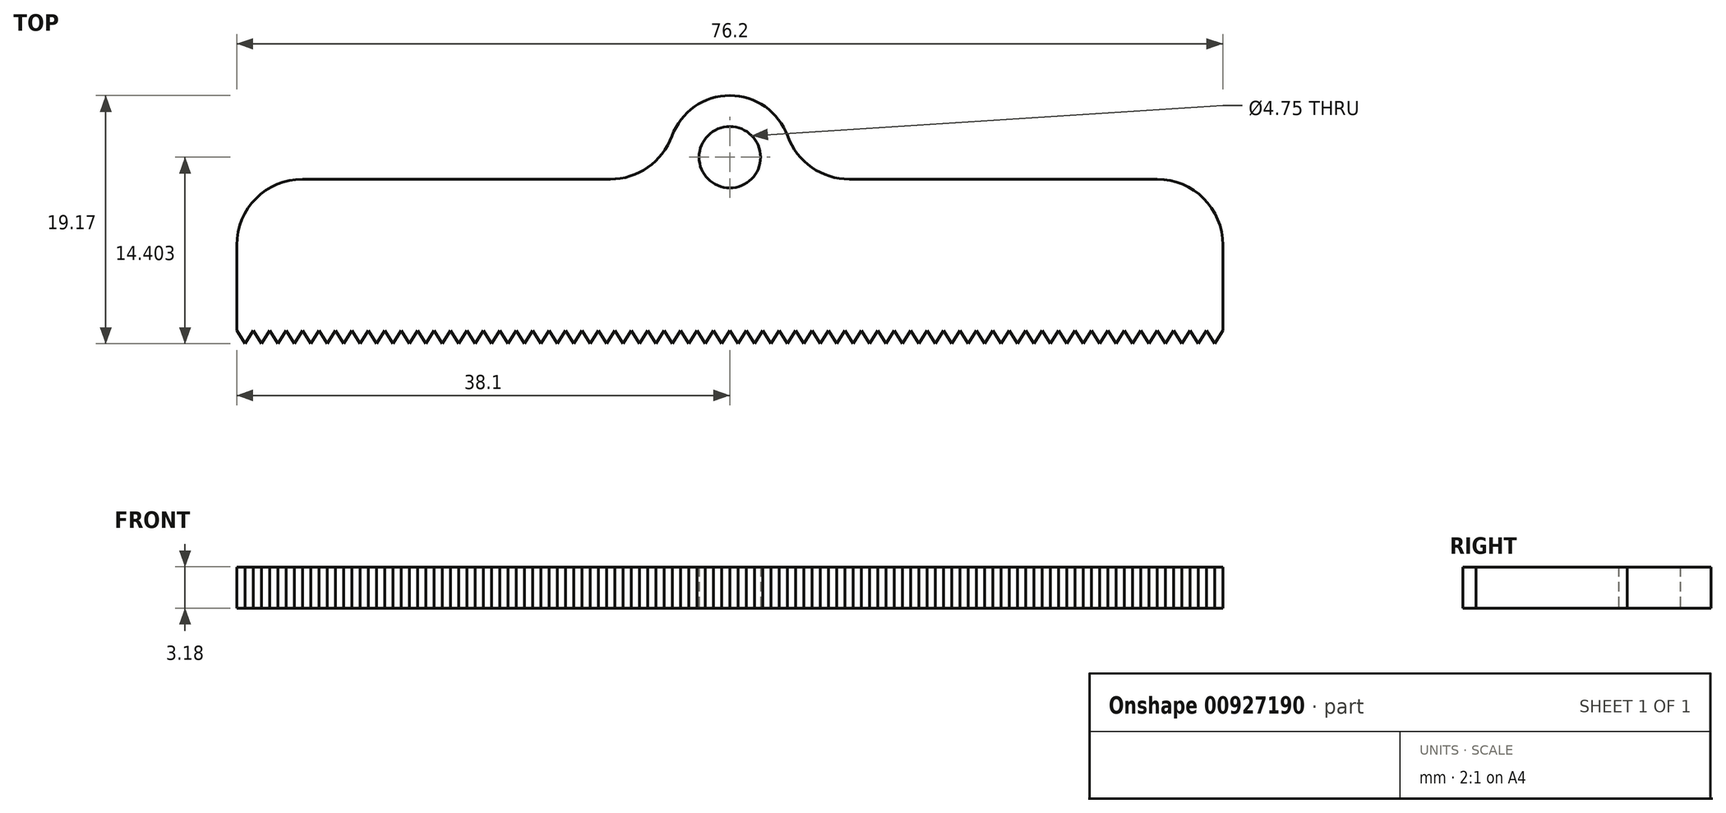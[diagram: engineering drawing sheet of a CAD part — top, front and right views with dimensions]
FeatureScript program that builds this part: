
annotation { "Feature Type Name" : "Feature", "Feature Type Description" : "" }
export const myFeature = defineFeature(function(context is Context, id is Id, definition is map)
    precondition{}
    {
        {
            var Q0;
            Q0=qCreatedBy(makeId("Top.planeOp"),FACE);
            var sketch = newSketch(context, id + "F0", { "sketchPlane" : qUnion([Q0])});
            skLineSegment(sketch, "E0.bottom", {"start": v(38.1, -9.52) * mm, "end": v(-38.1, -9.53) * mm});
            skLineSegment(sketch, "E0.left", {"start": v(38.1, -9.52) * mm, "end": v(38.1, -1.9) * mm});
            skLineSegment(sketch, "E0.right", {"start": v(-38.1, -9.53) * mm, "end": v(-38.1, -1.9) * mm});
            skPoint(sketch, "E0.middle", {"position": v(0, 0) * mm});
            skLineSegment(sketch, "E1", {"start": v(-33.02, 3.17) * mm, "end": v(-9.24, 3.17) * mm});
            skPoint(sketch, "E2.orphan", {"position": v(-38.1, 9.52) * mm});
            skPoint(sketch, "E3.orphan", {"position": v(38.1, 9.53) * mm});
            skLineSegment(sketch, "E4.trimOffspring", {"start": v(9.24, 3.17) * mm, "end": v(33.02, 3.17) * mm});
            skPoint(sketch, "E5.visualSharp", {"position": v(-38.1, 3.17) * mm});
            skArc(sketch, "E5.filletArc", {"start": v(-33.02, 3.18) * mm, "mid": v(-36.61, 1.69) * mm, "end": v(-38.1, -1.9) * mm});
            skPoint(sketch, "E6.visualSharp", {"position": v(38.1, 3.17) * mm});
            skArc(sketch, "E6.filletArc", {"start": v(38.1, -1.9) * mm, "mid": v(36.61, 1.69) * mm, "end": v(33.02, 3.18) * mm});
            skCircle(sketch, "E7", {"center": v(0, 4.87) * mm, "radius": 2.37 * mm});
            skArc(sketch, "E8", {"start": v(4.47, 6.5) * mm, "mid": v(0, 9.64) * mm, "end": v(-4.47, 6.5) * mm});
            skPoint(sketch, "E9.visualSharp", {"position": v(-4.45, 3.18) * mm});
            skArc(sketch, "E9.filletArc", {"start": v(-9.24, 3.18) * mm, "mid": v(-6.33, 4.1) * mm, "end": v(-4.47, 6.5) * mm});
            skPoint(sketch, "E10.visualSharp", {"position": v(4.45, 3.18) * mm});
            skArc(sketch, "E10.filletArc", {"start": v(4.47, 6.5) * mm, "mid": v(6.33, 4.1) * mm, "end": v(9.24, 3.17) * mm});
            skSolve(sketch);
        }
        {
            var Q0;
            Q0=makeQuery(id+"F0.imprint","IMPRINT",FACE,{"disambiguationData":[TD([[makeQuery(id+"F0.imprint","IMPRINT",EDGE,{"derivedFrom":sQuery(id+"F0.wireOp",EDGE,"E0.bottom")}),-1.0]])]});
            extrude(context, id + "F1", {"entities" : qUnion([Q0]), "depth" : 3.17 * mm, "offsetDistance" : 25.4 * mm});
        }
        {
            var Q0;
            Q0=makeQuery(id+"F1.opExtrude","CAP_FACE",FACE,{"disambiguationData":[OSD([sQuery(id+"F0.wireOp",EDGE,"E0.bottom"),sQuery(id+"F0.wireOp",EDGE,"E0.left"),sQuery(id+"F0.wireOp",EDGE,"E0.right"),sQuery(id+"F0.wireOp",EDGE,"E1"),sQuery(id+"F0.wireOp",EDGE,"E4.trimOffspring"),sQuery(id+"F0.wireOp",EDGE,"E5.filletArc"),sQuery(id+"F0.wireOp",EDGE,"E6.filletArc"),sQuery(id+"F0.wireOp",EDGE,"E7"),sQuery(id+"F0.wireOp",EDGE,"E8"),sQuery(id+"F0.wireOp",EDGE,"E9.filletArc"),sQuery(id+"F0.wireOp",EDGE,"E10.filletArc")])],"isStart":false});
            var sketch = newSketch(context, id + "F2", { "sketchPlane" : qUnion([Q0])});
            skLineSegment(sketch, "E11", {"start": v(-38.73, -9.53) * mm, "end": v(-38.1, -8.5) * mm});
            skLineSegment(sketch, "E12", {"start": v(-38.1, -8.5) * mm, "end": v(-37.46, -9.53) * mm});
            skLineSegment(sketch, "E13.1.0.0", {"start": v(-37.47, -9.53) * mm, "end": v(-36.83, -8.5) * mm});
            skLineSegment(sketch, "E13.1.0.1", {"start": v(-36.83, -8.5) * mm, "end": v(-36.2, -9.53) * mm});
            skLineSegment(sketch, "E13.2.0.0", {"start": v(-36.2, -9.53) * mm, "end": v(-35.56, -8.5) * mm});
            skLineSegment(sketch, "E13.2.0.1", {"start": v(-35.56, -8.5) * mm, "end": v(-34.93, -9.53) * mm});
            skLineSegment(sketch, "E13.3.0.0", {"start": v(-34.93, -9.53) * mm, "end": v(-34.3, -8.5) * mm});
            skLineSegment(sketch, "E13.3.0.1", {"start": v(-34.3, -8.5) * mm, "end": v(-33.66, -9.53) * mm});
            skLineSegment(sketch, "E13.4.0.0", {"start": v(-33.66, -9.53) * mm, "end": v(-33.02, -8.5) * mm});
            skLineSegment(sketch, "E13.4.0.1", {"start": v(-33.02, -8.5) * mm, "end": v(-32.39, -9.53) * mm});
            skLineSegment(sketch, "E13.5.0.0", {"start": v(-32.39, -9.53) * mm, "end": v(-31.75, -8.5) * mm});
            skLineSegment(sketch, "E13.5.0.1", {"start": v(-31.75, -8.5) * mm, "end": v(-31.12, -9.53) * mm});
            skLineSegment(sketch, "E13.6.0.0", {"start": v(-31.12, -9.53) * mm, "end": v(-30.48, -8.5) * mm});
            skLineSegment(sketch, "E13.6.0.1", {"start": v(-30.48, -8.5) * mm, "end": v(-29.85, -9.53) * mm});
            skLineSegment(sketch, "E13.7.0.0", {"start": v(-29.85, -9.53) * mm, "end": v(-29.21, -8.5) * mm});
            skLineSegment(sketch, "E13.7.0.1", {"start": v(-29.21, -8.5) * mm, "end": v(-28.58, -9.53) * mm});
            skLineSegment(sketch, "E13.8.0.0", {"start": v(-28.58, -9.53) * mm, "end": v(-27.94, -8.5) * mm});
            skLineSegment(sketch, "E13.8.0.1", {"start": v(-27.94, -8.5) * mm, "end": v(-27.3, -9.53) * mm});
            skLineSegment(sketch, "E13.9.0.0", {"start": v(-27.3, -9.53) * mm, "end": v(-26.67, -8.5) * mm});
            skLineSegment(sketch, "E13.9.0.1", {"start": v(-26.67, -8.5) * mm, "end": v(-26.04, -9.53) * mm});
            skLineSegment(sketch, "E13.10.0.0", {"start": v(-26.04, -9.53) * mm, "end": v(-25.4, -8.5) * mm});
            skLineSegment(sketch, "E13.10.0.1", {"start": v(-25.4, -8.5) * mm, "end": v(-24.77, -9.53) * mm});
            skLineSegment(sketch, "E13.11.0.0", {"start": v(-24.77, -9.53) * mm, "end": v(-24.13, -8.5) * mm});
            skLineSegment(sketch, "E13.11.0.1", {"start": v(-24.13, -8.5) * mm, "end": v(-23.5, -9.53) * mm});
            skLineSegment(sketch, "E13.12.0.0", {"start": v(-23.5, -9.53) * mm, "end": v(-22.86, -8.5) * mm});
            skLineSegment(sketch, "E13.12.0.1", {"start": v(-22.86, -8.5) * mm, "end": v(-22.23, -9.53) * mm});
            skLineSegment(sketch, "E13.13.0.0", {"start": v(-22.23, -9.53) * mm, "end": v(-21.6, -8.5) * mm});
            skLineSegment(sketch, "E13.13.0.1", {"start": v(-21.6, -8.5) * mm, "end": v(-20.96, -9.53) * mm});
            skLineSegment(sketch, "E13.14.0.0", {"start": v(-20.96, -9.53) * mm, "end": v(-20.32, -8.5) * mm});
            skLineSegment(sketch, "E13.14.0.1", {"start": v(-20.32, -8.5) * mm, "end": v(-19.69, -9.53) * mm});
            skLineSegment(sketch, "E13.15.0.0", {"start": v(-19.69, -9.53) * mm, "end": v(-19.05, -8.5) * mm});
            skLineSegment(sketch, "E13.15.0.1", {"start": v(-19.05, -8.5) * mm, "end": v(-18.42, -9.53) * mm});
            skLineSegment(sketch, "E13.16.0.0", {"start": v(-18.42, -9.53) * mm, "end": v(-17.78, -8.5) * mm});
            skLineSegment(sketch, "E13.16.0.1", {"start": v(-17.78, -8.5) * mm, "end": v(-17.15, -9.53) * mm});
            skLineSegment(sketch, "E13.17.0.0", {"start": v(-17.15, -9.53) * mm, "end": v(-16.51, -8.5) * mm});
            skLineSegment(sketch, "E13.17.0.1", {"start": v(-16.51, -8.5) * mm, "end": v(-15.88, -9.53) * mm});
            skLineSegment(sketch, "E13.18.0.0", {"start": v(-15.88, -9.53) * mm, "end": v(-15.24, -8.5) * mm});
            skLineSegment(sketch, "E13.18.0.1", {"start": v(-15.24, -8.5) * mm, "end": v(-14.6, -9.53) * mm});
            skLineSegment(sketch, "E13.19.0.0", {"start": v(-14.6, -9.53) * mm, "end": v(-13.97, -8.5) * mm});
            skLineSegment(sketch, "E13.19.0.1", {"start": v(-13.97, -8.5) * mm, "end": v(-13.34, -9.53) * mm});
            skLineSegment(sketch, "E13.20.0.0", {"start": v(-13.34, -9.53) * mm, "end": v(-12.7, -8.5) * mm});
            skLineSegment(sketch, "E13.20.0.1", {"start": v(-12.7, -8.5) * mm, "end": v(-12.07, -9.53) * mm});
            skLineSegment(sketch, "E13.21.0.0", {"start": v(-12.07, -9.53) * mm, "end": v(-11.43, -8.5) * mm});
            skLineSegment(sketch, "E13.21.0.1", {"start": v(-11.43, -8.5) * mm, "end": v(-10.8, -9.53) * mm});
            skLineSegment(sketch, "E13.22.0.0", {"start": v(-10.8, -9.53) * mm, "end": v(-10.16, -8.5) * mm});
            skLineSegment(sketch, "E13.22.0.1", {"start": v(-10.16, -8.5) * mm, "end": v(-9.53, -9.53) * mm});
            skLineSegment(sketch, "E13.23.0.0", {"start": v(-9.53, -9.53) * mm, "end": v(-8.9, -8.5) * mm});
            skLineSegment(sketch, "E13.23.0.1", {"start": v(-8.9, -8.5) * mm, "end": v(-8.26, -9.53) * mm});
            skLineSegment(sketch, "E13.24.0.0", {"start": v(-8.26, -9.53) * mm, "end": v(-7.62, -8.5) * mm});
            skLineSegment(sketch, "E13.24.0.1", {"start": v(-7.62, -8.5) * mm, "end": v(-6.99, -9.53) * mm});
            skLineSegment(sketch, "E13.25.0.0", {"start": v(-6.99, -9.53) * mm, "end": v(-6.35, -8.5) * mm});
            skLineSegment(sketch, "E13.25.0.1", {"start": v(-6.35, -8.5) * mm, "end": v(-5.72, -9.53) * mm});
            skLineSegment(sketch, "E13.26.0.0", {"start": v(-5.72, -9.53) * mm, "end": v(-5.08, -8.5) * mm});
            skLineSegment(sketch, "E13.26.0.1", {"start": v(-5.08, -8.5) * mm, "end": v(-4.45, -9.53) * mm});
            skLineSegment(sketch, "E13.27.0.0", {"start": v(-4.45, -9.53) * mm, "end": v(-3.81, -8.5) * mm});
            skLineSegment(sketch, "E13.27.0.1", {"start": v(-3.81, -8.5) * mm, "end": v(-3.18, -9.53) * mm});
            skLineSegment(sketch, "E13.28.0.0", {"start": v(-3.18, -9.53) * mm, "end": v(-2.54, -8.5) * mm});
            skLineSegment(sketch, "E13.28.0.1", {"start": v(-2.54, -8.5) * mm, "end": v(-1.9, -9.53) * mm});
            skLineSegment(sketch, "E13.29.0.0", {"start": v(-1.9, -9.53) * mm, "end": v(-1.27, -8.5) * mm});
            skLineSegment(sketch, "E13.29.0.1", {"start": v(-1.27, -8.5) * mm, "end": v(-0.64, -9.53) * mm});
            skLineSegment(sketch, "E13.30.0.0", {"start": v(-0.64, -9.53) * mm, "end": v(0, -8.5) * mm});
            skLineSegment(sketch, "E13.30.0.1", {"start": v(0, -8.5) * mm, "end": v(0.63, -9.53) * mm});
            skLineSegment(sketch, "E13.31.0.0", {"start": v(0.63, -9.53) * mm, "end": v(1.27, -8.5) * mm});
            skLineSegment(sketch, "E13.31.0.1", {"start": v(1.27, -8.5) * mm, "end": v(1.9, -9.53) * mm});
            skLineSegment(sketch, "E13.32.0.0", {"start": v(1.9, -9.53) * mm, "end": v(2.54, -8.5) * mm});
            skLineSegment(sketch, "E13.32.0.1", {"start": v(2.54, -8.5) * mm, "end": v(3.17, -9.53) * mm});
            skLineSegment(sketch, "E13.33.0.0", {"start": v(3.17, -9.53) * mm, "end": v(3.8, -8.5) * mm});
            skLineSegment(sketch, "E13.33.0.1", {"start": v(3.8, -8.5) * mm, "end": v(4.44, -9.53) * mm});
            skLineSegment(sketch, "E13.34.0.0", {"start": v(4.44, -9.53) * mm, "end": v(5.08, -8.5) * mm});
            skLineSegment(sketch, "E13.34.0.1", {"start": v(5.08, -8.5) * mm, "end": v(5.71, -9.53) * mm});
            skLineSegment(sketch, "E13.35.0.0", {"start": v(5.71, -9.53) * mm, "end": v(6.35, -8.5) * mm});
            skLineSegment(sketch, "E13.35.0.1", {"start": v(6.35, -8.5) * mm, "end": v(6.98, -9.53) * mm});
            skLineSegment(sketch, "E13.36.0.0", {"start": v(6.98, -9.53) * mm, "end": v(7.62, -8.5) * mm});
            skLineSegment(sketch, "E13.36.0.1", {"start": v(7.62, -8.5) * mm, "end": v(8.25, -9.53) * mm});
            skLineSegment(sketch, "E13.37.0.0", {"start": v(8.25, -9.53) * mm, "end": v(8.89, -8.5) * mm});
            skLineSegment(sketch, "E13.37.0.1", {"start": v(8.89, -8.5) * mm, "end": v(9.52, -9.53) * mm});
            skLineSegment(sketch, "E13.38.0.0", {"start": v(9.52, -9.53) * mm, "end": v(10.16, -8.5) * mm});
            skLineSegment(sketch, "E13.38.0.1", {"start": v(10.16, -8.5) * mm, "end": v(10.8, -9.53) * mm});
            skLineSegment(sketch, "E13.39.0.0", {"start": v(10.8, -9.53) * mm, "end": v(11.43, -8.5) * mm});
            skLineSegment(sketch, "E13.39.0.1", {"start": v(11.43, -8.5) * mm, "end": v(12.06, -9.53) * mm});
            skLineSegment(sketch, "E13.40.0.0", {"start": v(12.06, -9.53) * mm, "end": v(12.7, -8.5) * mm});
            skLineSegment(sketch, "E13.40.0.1", {"start": v(12.7, -8.5) * mm, "end": v(13.33, -9.53) * mm});
            skLineSegment(sketch, "E13.41.0.0", {"start": v(13.33, -9.53) * mm, "end": v(13.97, -8.5) * mm});
            skLineSegment(sketch, "E13.41.0.1", {"start": v(13.97, -8.5) * mm, "end": v(14.6, -9.53) * mm});
            skLineSegment(sketch, "E13.42.0.0", {"start": v(14.6, -9.53) * mm, "end": v(15.24, -8.5) * mm});
            skLineSegment(sketch, "E13.42.0.1", {"start": v(15.24, -8.5) * mm, "end": v(15.87, -9.53) * mm});
            skLineSegment(sketch, "E13.43.0.0", {"start": v(15.87, -9.53) * mm, "end": v(16.5, -8.5) * mm});
            skLineSegment(sketch, "E13.43.0.1", {"start": v(16.5, -8.5) * mm, "end": v(17.14, -9.53) * mm});
            skLineSegment(sketch, "E13.44.0.0", {"start": v(17.14, -9.53) * mm, "end": v(17.78, -8.5) * mm});
            skLineSegment(sketch, "E13.44.0.1", {"start": v(17.78, -8.5) * mm, "end": v(18.41, -9.53) * mm});
            skLineSegment(sketch, "E13.45.0.0", {"start": v(18.41, -9.53) * mm, "end": v(19.05, -8.5) * mm});
            skLineSegment(sketch, "E13.45.0.1", {"start": v(19.05, -8.5) * mm, "end": v(19.68, -9.53) * mm});
            skLineSegment(sketch, "E13.46.0.0", {"start": v(19.68, -9.53) * mm, "end": v(20.32, -8.5) * mm});
            skLineSegment(sketch, "E13.46.0.1", {"start": v(20.32, -8.5) * mm, "end": v(20.95, -9.53) * mm});
            skLineSegment(sketch, "E13.47.0.0", {"start": v(20.95, -9.53) * mm, "end": v(21.59, -8.5) * mm});
            skLineSegment(sketch, "E13.47.0.1", {"start": v(21.59, -8.5) * mm, "end": v(22.22, -9.53) * mm});
            skLineSegment(sketch, "E13.48.0.0", {"start": v(22.22, -9.53) * mm, "end": v(22.86, -8.5) * mm});
            skLineSegment(sketch, "E13.48.0.1", {"start": v(22.86, -8.5) * mm, "end": v(23.5, -9.53) * mm});
            skLineSegment(sketch, "E13.49.0.0", {"start": v(23.5, -9.53) * mm, "end": v(24.13, -8.5) * mm});
            skLineSegment(sketch, "E13.49.0.1", {"start": v(24.13, -8.5) * mm, "end": v(24.76, -9.53) * mm});
            skLineSegment(sketch, "E13.50.0.0", {"start": v(24.76, -9.53) * mm, "end": v(25.4, -8.5) * mm});
            skLineSegment(sketch, "E13.50.0.1", {"start": v(25.4, -8.5) * mm, "end": v(26.03, -9.53) * mm});
            skLineSegment(sketch, "E13.51.0.0", {"start": v(26.03, -9.53) * mm, "end": v(26.67, -8.5) * mm});
            skLineSegment(sketch, "E13.51.0.1", {"start": v(26.67, -8.5) * mm, "end": v(27.3, -9.53) * mm});
            skLineSegment(sketch, "E13.52.0.0", {"start": v(27.3, -9.53) * mm, "end": v(27.94, -8.5) * mm});
            skLineSegment(sketch, "E13.52.0.1", {"start": v(27.94, -8.5) * mm, "end": v(28.57, -9.53) * mm});
            skLineSegment(sketch, "E13.53.0.0", {"start": v(28.57, -9.53) * mm, "end": v(29.2, -8.5) * mm});
            skLineSegment(sketch, "E13.53.0.1", {"start": v(29.2, -8.5) * mm, "end": v(29.84, -9.53) * mm});
            skLineSegment(sketch, "E13.54.0.0", {"start": v(29.84, -9.53) * mm, "end": v(30.48, -8.5) * mm});
            skLineSegment(sketch, "E13.54.0.1", {"start": v(30.48, -8.5) * mm, "end": v(31.11, -9.53) * mm});
            skLineSegment(sketch, "E13.55.0.0", {"start": v(31.11, -9.53) * mm, "end": v(31.75, -8.5) * mm});
            skLineSegment(sketch, "E13.55.0.1", {"start": v(31.75, -8.5) * mm, "end": v(32.38, -9.53) * mm});
            skLineSegment(sketch, "E13.56.0.0", {"start": v(32.38, -9.53) * mm, "end": v(33.02, -8.5) * mm});
            skLineSegment(sketch, "E13.56.0.1", {"start": v(33.02, -8.5) * mm, "end": v(33.65, -9.53) * mm});
            skLineSegment(sketch, "E13.57.0.0", {"start": v(33.65, -9.53) * mm, "end": v(34.29, -8.5) * mm});
            skLineSegment(sketch, "E13.57.0.1", {"start": v(34.29, -8.5) * mm, "end": v(34.92, -9.53) * mm});
            skLineSegment(sketch, "E13.58.0.0", {"start": v(34.92, -9.53) * mm, "end": v(35.56, -8.5) * mm});
            skLineSegment(sketch, "E13.58.0.1", {"start": v(35.56, -8.5) * mm, "end": v(36.2, -9.53) * mm});
            skLineSegment(sketch, "E13.59.0.0", {"start": v(36.2, -9.53) * mm, "end": v(36.83, -8.5) * mm});
            skLineSegment(sketch, "E13.59.0.1", {"start": v(36.83, -8.5) * mm, "end": v(37.46, -9.53) * mm});
            skLineSegment(sketch, "E13.direction1", {"start": v(-38.74, -9.53) * mm, "end": v(-37.47, -9.53) * mm, "construction": true});
            skLineSegment(sketch, "E14.top", {"start": v(-38.1, -14.15) * mm, "end": v(38.1, -14.15) * mm});
            skLineSegment(sketch, "E14.left", {"start": v(-38.1, -8.5) * mm, "end": v(-38.1, -14.15) * mm});
            skLineSegment(sketch, "E14.right", {"start": v(38.1, -8.5) * mm, "end": v(38.1, -14.15) * mm});
            skLineSegment(sketch, "E15", {"start": v(37.46, -9.52) * mm, "end": v(38.1, -8.5) * mm});
            skSolve(sketch);
        }
        {
            var Q0;
            Q0 = qSketchRegion(id + "F2", true);
            extrude(context, id + "F3", {"entities" : qUnion([Q0]), "operationType" : NewBodyOperationType.REMOVE, "oppositeDirection" : true, "depth" : 25.4 * mm, "offsetDistance" : 25.4 * mm});
        }
    });
